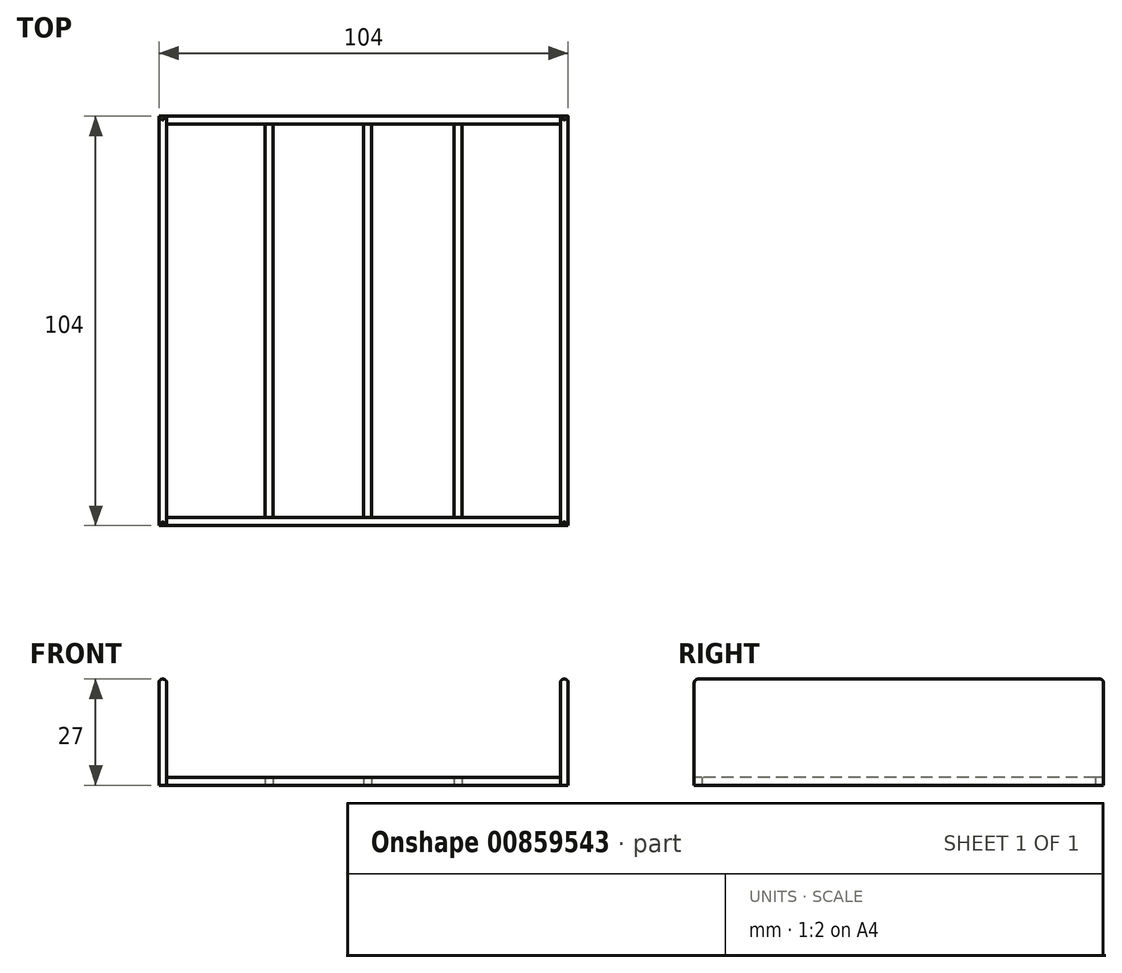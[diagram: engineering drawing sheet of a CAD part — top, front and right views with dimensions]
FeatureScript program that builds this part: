
annotation { "Feature Type Name" : "Feature", "Feature Type Description" : "" }
export const myFeature = defineFeature(function(context is Context, id is Id, definition is map)
    precondition{}
    {
        {
            var Q0;
            Q0=qCreatedBy(makeId("Top.planeOp"),FACE);
            var sketch = newSketch(context, id + "F0", { "sketchPlane" : qUnion([Q0])});
            skLineSegment(sketch, "E0.bottom", {"start": v(-1, 54) * mm, "end": v(1, 54) * mm});
            skLineSegment(sketch, "E0.top", {"start": v(-1, -50) * mm, "end": v(1, -50) * mm});
            skLineSegment(sketch, "E0.left", {"start": v(-1, 54) * mm, "end": v(-1, -50) * mm});
            skLineSegment(sketch, "E0.right", {"start": v(1, 54) * mm, "end": v(1, -50) * mm});
            skSolve(sketch);
        }
        {
            var Q0;
            Q0 = qSketchRegion(id + "F0", true);
            extrude(context, id + "F1", {"entities" : qUnion([Q0]), "depth" : 27 * mm, "offsetDistance" : 25 * mm});
        }
        {
            var Q0;
            Q0=makeQuery(id+"F1.opExtrude","CAP_FACE",FACE,{"disambiguationData":[OSD([sQuery(id+"F0.wireOp",EDGE,"E0.bottom"),sQuery(id+"F0.wireOp",EDGE,"E0.top"),sQuery(id+"F0.wireOp",EDGE,"E0.left"),sQuery(id+"F0.wireOp",EDGE,"E0.right")])],"isStart":false});
            fillet(context, id + "F2", {"entities" : qUnion([Q0]), "radius" : 1 * mm, "tangentPropagation" : true, "allowEdgeOverflow" : false});
        }
        {
            var Q0;
            Q0=makeQuery(id+"F1.opExtrude","SWEPT_BODY",BODY,{"disambiguationData":[OSD([sQuery(id+"F0.wireOp",EDGE,"E0.bottom"),sQuery(id+"F0.wireOp",EDGE,"E0.top"),sQuery(id+"F0.wireOp",EDGE,"E0.left"),sQuery(id+"F0.wireOp",EDGE,"E0.right")])]});
            var Q1;
            Q1=makeQuery(id+"F1.opExtrude","SWEPT_FACE",FACE,{"disambiguationData":[OSD([sQuery(id+"F0.wireOp",EDGE,"E0.right")])]});
            transform(context, id + "F3", {"entities" : qUnion([Q0]), "transformType" : TransformType.TRANSLATION_DISTANCE, "transformDirection" : qUnion([Q1]), "distance" : 50 * mm, "makeCopy" : false});
        }
        {
            var Q0;
            Q0=qCreatedBy(makeId("Top.planeOp"),FACE);
            var sketch = newSketch(context, id + "F4", { "sketchPlane" : qUnion([Q0])});
            skLineSegment(sketch, "E1.bottom", {"start": v(-53, 54) * mm, "end": v(-51, 54) * mm});
            skLineSegment(sketch, "E1.top", {"start": v(-53, -50) * mm, "end": v(-51, -50) * mm});
            skLineSegment(sketch, "E1.left", {"start": v(-53, 54) * mm, "end": v(-53, -50) * mm});
            skLineSegment(sketch, "E1.right", {"start": v(-51, 54) * mm, "end": v(-51, -50) * mm});
            skSolve(sketch);
        }
        {
            var Q0;
            Q0 = qSketchRegion(id + "F4", true);
            extrude(context, id + "F5", {"entities" : qUnion([Q0]), "depth" : 27 * mm, "offsetDistance" : 25 * mm});
        }
        {
            var Q0;
            Q0=makeQuery(id+"F5.opExtrude","CAP_FACE",FACE,{"disambiguationData":[OSD([sQuery(id+"F4.wireOp",EDGE,"E1.bottom"),sQuery(id+"F4.wireOp",EDGE,"E1.top"),sQuery(id+"F4.wireOp",EDGE,"E1.left"),sQuery(id+"F4.wireOp",EDGE,"E1.right")])],"isStart":false});
            fillet(context, id + "F6", {"entities" : qUnion([Q0]), "radius" : 1 * mm, "tangentPropagation" : true, "allowEdgeOverflow" : false});
        }
        {
            var Q0;
            Q0=qCreatedBy(makeId("Top.planeOp"),FACE);
            var sketch = newSketch(context, id + "F7", { "sketchPlane" : qUnion([Q0])});
            skLineSegment(sketch, "E2.bottom", {"start": v(-26, 50) * mm, "end": v(-24, 50) * mm});
            skLineSegment(sketch, "E2.top", {"start": v(-26, -50) * mm, "end": v(-24, -50) * mm});
            skLineSegment(sketch, "E2.left", {"start": v(-26, 50) * mm, "end": v(-26, -50) * mm});
            skLineSegment(sketch, "E2.right", {"start": v(-24, 50) * mm, "end": v(-24, -50) * mm});
            skSolve(sketch);
        }
        {
            var Q0;
            Q0 = qSketchRegion(id + "F7", true);
            extrude(context, id + "F8", {"entities" : qUnion([Q0]), "depth" : 2 * mm, "offsetDistance" : 25 * mm});
        }
        {
            var Q0;
            Q0=qCreatedBy(makeId("Top.planeOp"),FACE);
            var sketch = newSketch(context, id + "F9", { "sketchPlane" : qUnion([Q0])});
            skLineSegment(sketch, "E3.bottom", {"start": v(22, 50) * mm, "end": v(24, 50) * mm});
            skLineSegment(sketch, "E3.top", {"start": v(22, -50) * mm, "end": v(24, -50) * mm});
            skLineSegment(sketch, "E3.left", {"start": v(22, 50) * mm, "end": v(22, -50) * mm});
            skLineSegment(sketch, "E3.right", {"start": v(24, 50) * mm, "end": v(24, -50) * mm});
            skSolve(sketch);
        }
        {
            var Q0;
            Q0 = qSketchRegion(id + "F9", true);
            extrude(context, id + "F10", {"entities" : qUnion([Q0]), "depth" : 2 * mm, "offsetDistance" : 25 * mm});
        }
        {
            var Q0;
            Q0=qCreatedBy(makeId("Top.planeOp"),FACE);
            var sketch = newSketch(context, id + "F11", { "sketchPlane" : qUnion([Q0])});
            skLineSegment(sketch, "E4.bottom", {"start": v(-1, 50) * mm, "end": v(1, 50) * mm});
            skLineSegment(sketch, "E4.top", {"start": v(-1, -50) * mm, "end": v(1, -50) * mm});
            skLineSegment(sketch, "E4.left", {"start": v(-1, 50) * mm, "end": v(-1, -50) * mm});
            skLineSegment(sketch, "E4.right", {"start": v(1, 50) * mm, "end": v(1, -50) * mm});
            skSolve(sketch);
        }
        {
            var Q0;
            Q0 = qSketchRegion(id + "F11", true);
            extrude(context, id + "F12", {"entities" : qUnion([Q0]), "depth" : 2 * mm, "offsetDistance" : 25 * mm});
        }
        {
            var Q0;
            Q0=makeQuery(id+"F12.opExtrude","SWEPT_BODY",BODY,{"disambiguationData":[OSD([sQuery(id+"F11.wireOp",EDGE,"E4.bottom"),sQuery(id+"F11.wireOp",EDGE,"E4.top"),sQuery(id+"F11.wireOp",EDGE,"E4.left"),sQuery(id+"F11.wireOp",EDGE,"E4.right")])]});
            var Q1;
            Q1=makeQuery(id+"F12.opExtrude","SWEPT_EDGE",EDGE,{"disambiguationData":[OSD([sQuery(id+"F11.wireOp",EDGE,"E4.top"),sQuery(id+"F11.wireOp",EDGE,"E4.left")])]});
            transform(context, id + "F13", {"entities" : qUnion([Q0]), "transformType" : TransformType.ROTATION, "transformAxis" : qUnion([Q1]), "angle" : 90 * degree, "makeCopy" : true});
        }
        {
            var Q0;
            Q0=makeQuery(id+"F13.opPattern","COPY",BODY,{"derivedFrom":makeQuery(id+"F12.opExtrude","SWEPT_BODY",BODY,{"disambiguationData":[OSD([sQuery(id+"F11.wireOp",EDGE,"E4.bottom"),sQuery(id+"F11.wireOp",EDGE,"E4.top"),sQuery(id+"F11.wireOp",EDGE,"E4.left"),sQuery(id+"F11.wireOp",EDGE,"E4.right")])]}),"instanceName":"1"});
            var Q1;
            Q1=makeQuery(id+"F13.opPattern","COPY",FACE,{"derivedFrom":makeQuery(id+"F12.opExtrude","SWEPT_FACE",FACE,{"disambiguationData":[OSD([sQuery(id+"F11.wireOp",EDGE,"E4.top")])]}),"instanceName":"1"});
            transform(context, id + "F14", {"entities" : qUnion([Q0]), "transformType" : TransformType.TRANSLATION_DISTANCE, "transformDirection" : qUnion([Q1]), "distance" : 50 * mm, "makeCopy" : false});
        }
        {
            var Q0;
            Q0=makeQuery(id+"F5.opExtrude","SWEPT_BODY",BODY,{"disambiguationData":[OSD([sQuery(id+"F4.wireOp",EDGE,"E1.bottom"),sQuery(id+"F4.wireOp",EDGE,"E1.top"),sQuery(id+"F4.wireOp",EDGE,"E1.left"),sQuery(id+"F4.wireOp",EDGE,"E1.right")])]});
            var Q1;
            Q1=makeQuery(id+"F5.opExtrude","SWEPT_FACE",FACE,{"disambiguationData":[OSD([sQuery(id+"F4.wireOp",EDGE,"E1.top")])]});
            transform(context, id + "F15", {"entities" : qUnion([Q0]), "transformType" : TransformType.TRANSLATION_DISTANCE, "transformDirection" : qUnion([Q1]), "distance" : 2 * mm, "makeCopy" : false});
        }
        {
            var Q0;
            Q0=makeQuery(id+"F1.opExtrude","SWEPT_BODY",BODY,{"disambiguationData":[OSD([sQuery(id+"F0.wireOp",EDGE,"E0.bottom"),sQuery(id+"F0.wireOp",EDGE,"E0.top"),sQuery(id+"F0.wireOp",EDGE,"E0.left"),sQuery(id+"F0.wireOp",EDGE,"E0.right")])]});
            var Q1;
            Q1=makeQuery(id+"F1.opExtrude","SWEPT_FACE",FACE,{"disambiguationData":[OSD([sQuery(id+"F0.wireOp",EDGE,"E0.top")])]});
            transform(context, id + "F16", {"entities" : qUnion([Q0]), "transformType" : TransformType.TRANSLATION_DISTANCE, "transformDirection" : qUnion([Q1]), "distance" : 2 * mm, "makeCopy" : false});
        }
        {
            var Q0;
            Q0=makeQuery(id+"F12.opExtrude","SWEPT_BODY",BODY,{"disambiguationData":[OSD([sQuery(id+"F11.wireOp",EDGE,"E4.bottom"),sQuery(id+"F11.wireOp",EDGE,"E4.top"),sQuery(id+"F11.wireOp",EDGE,"E4.left"),sQuery(id+"F11.wireOp",EDGE,"E4.right")])]});
            var Q1;
            Q1=makeQuery(id+"F12.opExtrude","SWEPT_EDGE",EDGE,{"disambiguationData":[OSD([sQuery(id+"F11.wireOp",EDGE,"E4.bottom"),sQuery(id+"F11.wireOp",EDGE,"E4.left")])]});
            transform(context, id + "F17", {"entities" : qUnion([Q0]), "transformType" : TransformType.ROTATION, "transformAxis" : qUnion([Q1]), "angle" : 90 * degree, "makeCopy" : true});
        }
        {
            var Q0;
            Q0=makeQuery(id+"F17.opPattern","COPY",BODY,{"derivedFrom":makeQuery(id+"F12.opExtrude","SWEPT_BODY",BODY,{"disambiguationData":[OSD([sQuery(id+"F11.wireOp",EDGE,"E4.bottom"),sQuery(id+"F11.wireOp",EDGE,"E4.top"),sQuery(id+"F11.wireOp",EDGE,"E4.left"),sQuery(id+"F11.wireOp",EDGE,"E4.right")])]}),"instanceName":"1"});
            var Q1;
            Q1=makeQuery(id+"F17.opPattern","COPY",FACE,{"derivedFrom":makeQuery(id+"F12.opExtrude","SWEPT_FACE",FACE,{"disambiguationData":[OSD([sQuery(id+"F11.wireOp",EDGE,"E4.left")])]}),"instanceName":"1"});
            transform(context, id + "F18", {"entities" : qUnion([Q0]), "transformType" : TransformType.TRANSLATION_DISTANCE, "transformDirection" : qUnion([Q1]), "distance" : 2 * mm, "makeCopy" : false});
        }
        {
            var Q0;
            Q0=makeQuery(id+"F17.opPattern","COPY",BODY,{"derivedFrom":makeQuery(id+"F12.opExtrude","SWEPT_BODY",BODY,{"disambiguationData":[OSD([sQuery(id+"F11.wireOp",EDGE,"E4.bottom"),sQuery(id+"F11.wireOp",EDGE,"E4.top"),sQuery(id+"F11.wireOp",EDGE,"E4.left"),sQuery(id+"F11.wireOp",EDGE,"E4.right")])]}),"instanceName":"1"});
            var Q1;
            Q1=makeQuery(id+"F17.opPattern","COPY",FACE,{"derivedFrom":makeQuery(id+"F12.opExtrude","SWEPT_FACE",FACE,{"disambiguationData":[OSD([sQuery(id+"F11.wireOp",EDGE,"E4.bottom")])]}),"instanceName":"1"});
            transform(context, id + "F19", {"entities" : qUnion([Q0]), "transformType" : TransformType.TRANSLATION_DISTANCE, "transformDirection" : qUnion([Q1]), "distance" : 50 * mm, "makeCopy" : false});
        }
    });
